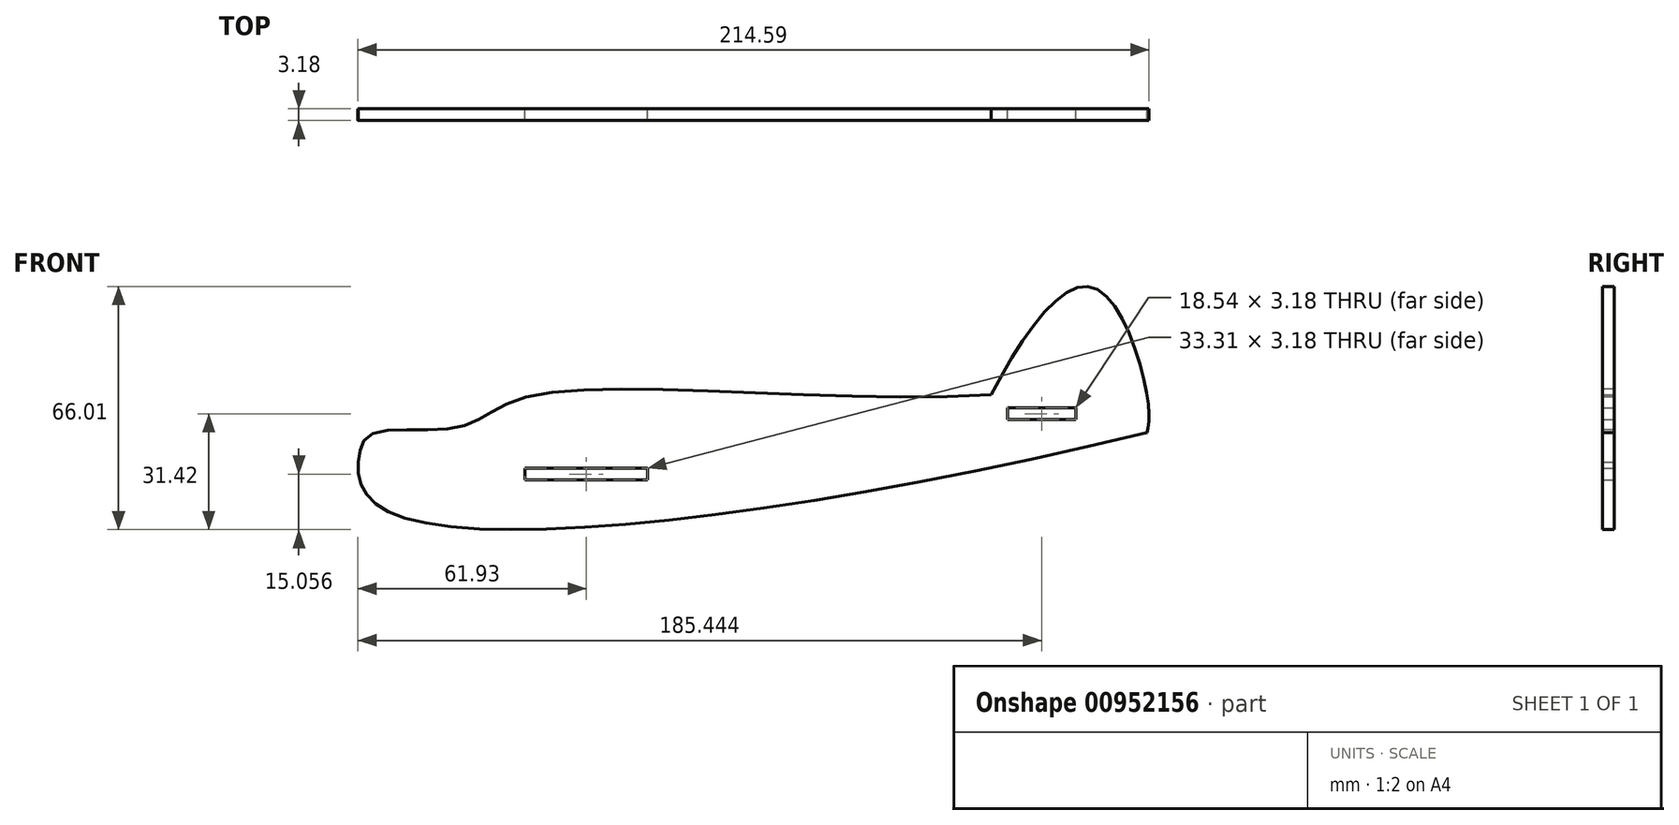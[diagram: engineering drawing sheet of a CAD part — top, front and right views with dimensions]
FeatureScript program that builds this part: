
annotation { "Feature Type Name" : "Feature", "Feature Type Description" : "" }
export const myFeature = defineFeature(function(context is Context, id is Id, definition is map)
    precondition{}
    {
        {
            var Q0;
            Q0=qCreatedBy(makeId("Front.planeOp"),FACE);
            var sketch = newSketch(context, id + "F0", { "sketchPlane" : qUnion([Q0])});
            skLineSegment(sketch, "E0.bottom", {"start": v(114.3, 50.8) * mm, "end": v(-114.3, 50.8) * mm, "construction": true});
            skLineSegment(sketch, "E0.top", {"start": v(114.3, -50.8) * mm, "end": v(-114.3, -50.8) * mm, "construction": true});
            skLineSegment(sketch, "E0.left", {"start": v(114.3, 50.8) * mm, "end": v(114.3, -50.8) * mm, "construction": true});
            skLineSegment(sketch, "E0.right", {"start": v(-114.3, 50.8) * mm, "end": v(-114.3, -50.8) * mm, "construction": true});
            skPoint(sketch, "E0.middle", {"position": v(0, 0) * mm});
            skFitSpline(sketch, "E1", {"points": [v(-108.55, -3.41) * mm, v(-100.66, -16.67) * mm, v(105.45, 4.59) * mm], "startDerivative": vector(-4.94, -71.2) * mm, "endDerivative": vector(364.97, 87.93) * mm});
            skFitSpline(sketch, "E2", {"points": [v(-108.55, -3.41) * mm, v(-105.08, 4.16) * mm, v(-81.4, 6.05) * mm, v(-63.1, 14.26) * mm, v(63.23, 14.9) * mm], "startDerivative": vector(8.95, 75.69) * mm, "endDerivative": vector(265.43, 17.83) * mm});
            skFitSpline(sketch, "E3", {"points": [v(63.23, 14.9) * mm, v(90.82, 44) * mm, v(105.45, 14.9) * mm, v(105.45, 4.59) * mm], "startDerivative": vector(60.55, 118) * mm, "endDerivative": vector(-7.58, -28.3) * mm});
            skLineSegment(sketch, "E4.bottom", {"start": v(-63.32, -5.07) * mm, "end": v(-30, -5.07) * mm});
            skLineSegment(sketch, "E4.top", {"start": v(-63.32, -8.24) * mm, "end": v(-30, -8.24) * mm});
            skLineSegment(sketch, "E4.left", {"start": v(-63.32, -5.07) * mm, "end": v(-63.32, -8.24) * mm});
            skLineSegment(sketch, "E4.right", {"start": v(-30, -5.07) * mm, "end": v(-30, -8.24) * mm});
            skLineSegment(sketch, "E5.bottom", {"start": v(67.58, 11.3) * mm, "end": v(86.12, 11.3) * mm});
            skLineSegment(sketch, "E5.top", {"start": v(67.58, 8.12) * mm, "end": v(86.12, 8.12) * mm});
            skLineSegment(sketch, "E5.left", {"start": v(67.58, 11.3) * mm, "end": v(67.58, 8.12) * mm});
            skLineSegment(sketch, "E5.right", {"start": v(86.12, 11.3) * mm, "end": v(86.12, 8.12) * mm});
            skSolve(sketch);
        }
        {
            var Q0;
            Q0=makeQuery(id+"F0.imprint","IMPRINT",FACE,{"disambiguationData":[TD([[makeQuery(id+"F0.imprint","IMPRINT",EDGE,{"derivedFrom":sQuery(id+"F0.wireOp",EDGE,"E1")}),1.0]])]});
            extrude(context, id + "F1", {"entities" : qUnion([Q0]), "depth" : 3.17 * mm, "offsetDistance" : 25.4 * mm});
        }
    });
